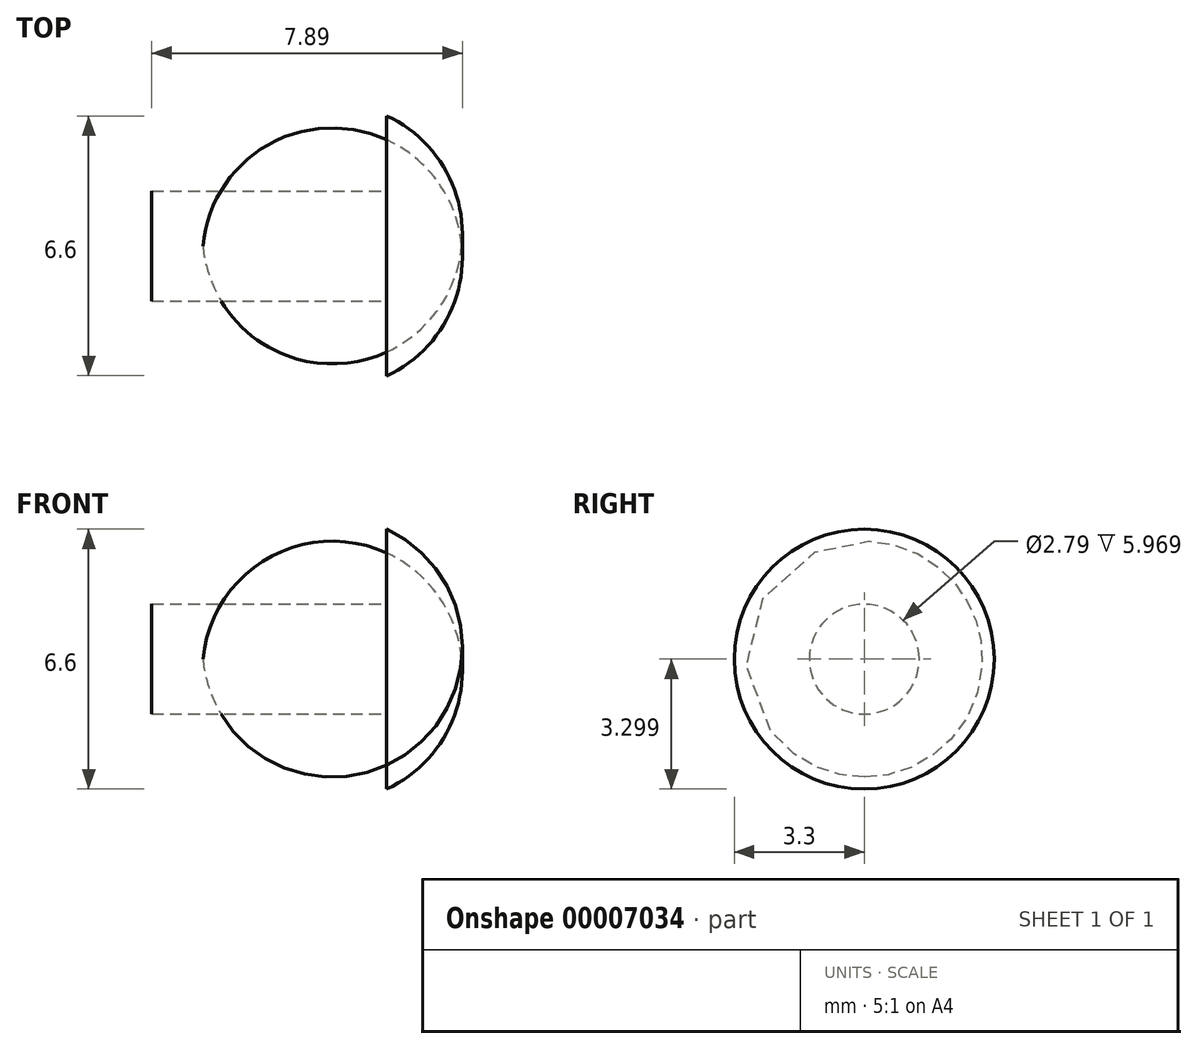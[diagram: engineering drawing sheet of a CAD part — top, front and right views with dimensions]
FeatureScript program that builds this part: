
annotation { "Feature Type Name" : "Feature", "Feature Type Description" : "" }
export const myFeature = defineFeature(function(context is Context, id is Id, definition is map)
    precondition{}
    {
        {
            var Q0;
            Q0=qCreatedBy(makeId("Front.planeOp"),FACE);
            var sketch = newSketch(context, id + "F0", { "sketchPlane" : qUnion([Q0])});
            skLineSegment(sketch, "E0", {"start": v(-53.43, 12.76) * mm, "end": v(-53.43, 9.46) * mm});
            skLineSegment(sketch, "E1", {"start": v(-53.43, 12.76) * mm, "end": v(-51.52, 12.76) * mm});
            skArc(sketch, "E2", {"start": v(-53.43, 9.46) * mm, "mid": v(-51.95, 10.8) * mm, "end": v(-51.52, 12.76) * mm});
            skSolve(sketch);
        }
        {
            var Q0;
            Q0 = qSketchRegion(id + "F0", true);
            var Q1;
            Q1=sQuery(id+"F0.wireOp",EDGE,"E1");
            revolve(context, id + "F1", {"entities" : qUnion([Q0]), "axis" : qUnion([Q1]), "revolveType" : RevolveType.FULL});
        }
        {
            var Q0;
            Q0=makeQuery(id+"F1.opRevolve","SWEPT_FACE",FACE,{"disambiguationData":[OSD([sQuery(id+"F0.wireOp",EDGE,"E0")])]});
            var sketch = newSketch(context, id + "F2", { "sketchPlane" : qUnion([Q0])});
            skCircle(sketch, "E3", {"center": v(0, 12.76) * mm, "radius": 1.4 * mm});
            skSolve(sketch);
        }
        {
            var Q0;
            Q0 = qSketchRegion(id + "F2", true);
            extrude(context, id + "F3", {"entities" : qUnion([Q0]), "operationType" : NewBodyOperationType.ADD, "depth" : 5.97 * mm});
        }
    });
